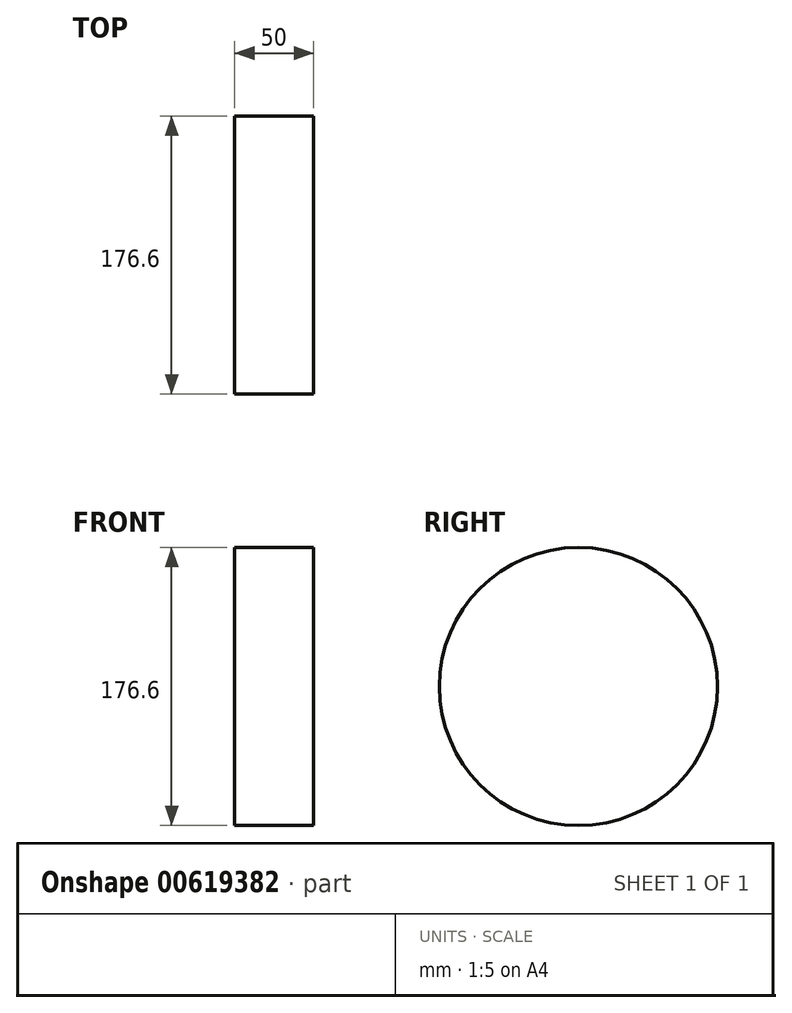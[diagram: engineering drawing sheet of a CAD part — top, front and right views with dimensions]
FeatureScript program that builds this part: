
annotation { "Feature Type Name" : "Feature", "Feature Type Description" : "" }
export const myFeature = defineFeature(function(context is Context, id is Id, definition is map)
    precondition{}
    {
        {
            var Q0;
            Q0=qCreatedBy(makeId("Right.planeOp"),FACE);
            var sketch = newSketch(context, id + "F0", { "sketchPlane" : qUnion([Q0])});
            skCircle(sketch, "E0", {"center": v(26.97, 49.2) * mm, "radius": 88.3 * mm});
            skSolve(sketch);
        }
        {
            var Q0;
            Q0 = qSketchRegion(id + "F0", true);
            extrude(context, id + "F1", {"entities" : qUnion([Q0]), "depth" : 25 * mm, "offsetDistance" : 25 * mm});
        }
        {
            var Q0;
            Q0=makeQuery(id+"F1.opExtrude","CAP_FACE",FACE,{"disambiguationData":[OSD([sQuery(id+"F0.wireOp",EDGE,"E0")])],"isStart":false});
            extrude(context, id + "F2", {"entities" : qUnion([Q0]), "operationType" : NewBodyOperationType.ADD, "depth" : 25 * mm, "offsetDistance" : 25 * mm});
        }
    });
